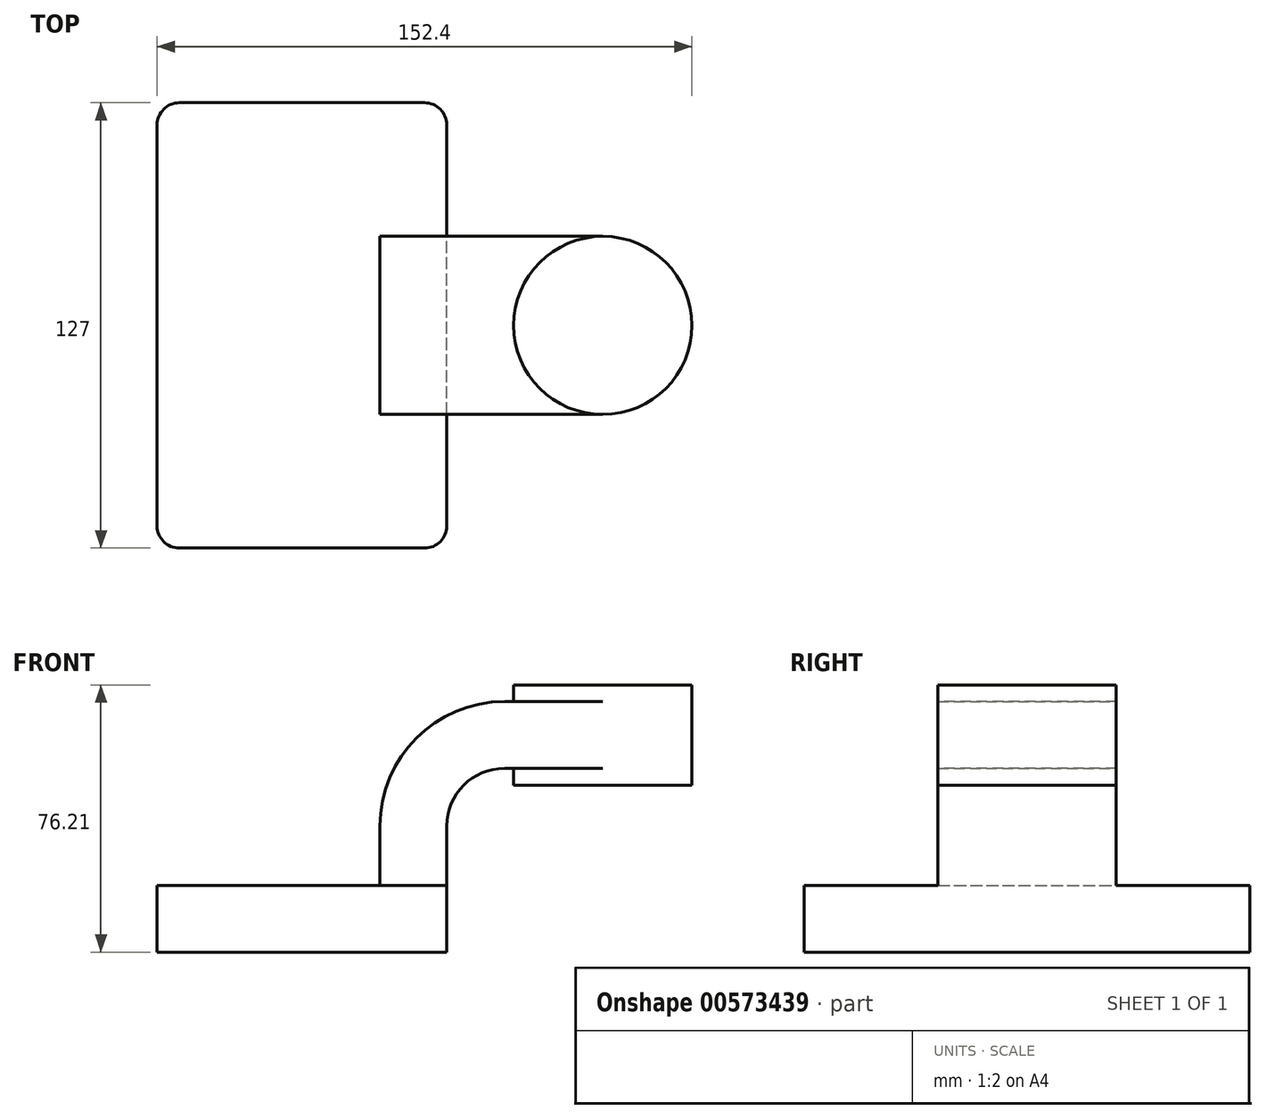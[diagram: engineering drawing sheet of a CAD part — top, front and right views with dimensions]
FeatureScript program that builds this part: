
annotation { "Feature Type Name" : "Feature", "Feature Type Description" : "" }
export const myFeature = defineFeature(function(context is Context, id is Id, definition is map)
    precondition{}
    {
        {
            var Q0;
            Q0=qCreatedBy(makeId("Front.planeOp"),FACE);
            var sketch = newSketch(context, id + "F0", { "sketchPlane" : qUnion([Q0])});
            skLineSegment(sketch, "E0.bottom", {"start": v(41.28, -9.52) * mm, "end": v(-41.28, -9.53) * mm});
            skLineSegment(sketch, "E0.top", {"start": v(41.28, 9.53) * mm, "end": v(-41.28, 9.53) * mm});
            skLineSegment(sketch, "E0.left", {"start": v(41.28, -9.52) * mm, "end": v(41.28, 9.53) * mm});
            skLineSegment(sketch, "E0.right", {"start": v(-41.28, -9.53) * mm, "end": v(-41.28, 9.53) * mm});
            skPoint(sketch, "E0.middle", {"position": v(0, 0) * mm});
            skLineSegment(sketch, "E1", {"start": v(41.28, 9.53) * mm, "end": v(41.28, 26.44) * mm});
            skLineSegment(sketch, "E2.bottom", {"start": v(111.12, 38.1) * mm, "end": v(60.32, 38.1) * mm});
            skLineSegment(sketch, "E2.top", {"start": v(111.12, 66.68) * mm, "end": v(60.32, 66.68) * mm});
            skLineSegment(sketch, "E2.left", {"start": v(111.12, 38.1) * mm, "end": v(111.12, 66.68) * mm});
            skLineSegment(sketch, "E2.right", {"start": v(60.32, 38.1) * mm, "end": v(60.32, 66.68) * mm});
            skPoint(sketch, "E2.middle", {"position": v(85.72, 52.39) * mm});
            skPoint(sketch, "E3.middle", {"position": v(111.12, 38.1) * mm});
            skLineSegment(sketch, "E4", {"start": v(15916.27, 15898.5) * mm, "end": v(15943.47, 15898.5) * mm});
            skArc(sketch, "E5", {"start": v(41.27, 26.44) * mm, "mid": v(46.09, 38.06) * mm, "end": v(57.7, 42.88) * mm});
            skLineSegment(sketch, "E6", {"start": v(57.7, 42.88) * mm, "end": v(85.72, 42.88) * mm});
            skPoint(sketch, "E6.endSnap0", {"position": v(85.72, 66.68) * mm});
            skLineSegment(sketch, "E7.0", {"start": v(57.7, 61.93) * mm, "end": v(85.72, 61.93) * mm});
            skArc(sketch, "E7.1", {"start": v(22.23, 26.44) * mm, "mid": v(32.62, 51.53) * mm, "end": v(57.7, 61.93) * mm});
            skLineSegment(sketch, "E7.2", {"start": v(22.22, 9.53) * mm, "end": v(22.22, 26.44) * mm});
            skFitSpline(sketch, "E8", {"points": [v(-41.28, 9.53) * mm, v(57.7, 61.93) * mm], "startDerivative": vector(-3.58, 69.63) * mm, "endDerivative": vector(173.12, -0.17) * mm});
            skLineSegment(sketch, "E9", {"start": v(85.72, 66.68) * mm, "end": v(85.72, 38.1) * mm});
            skSolve(sketch);
        }
        {
            var Q0;
            Q0=makeQuery(id+"F0.imprint","IMPRINT",FACE,{"disambiguationData":[TD([[makeQuery(id+"F0.imprint","IMPRINT",EDGE,{"derivedFrom":sQuery(id+"F0.wireOp",EDGE,"E0.bottom")}),-1.0]])]});
            extrude(context, id + "F1", {"entities" : qUnion([Q0]), "endBound" : BoundingType.SYMMETRIC, "depth" : 127 * mm, "offsetDistance" : 25.4 * mm});
        }
        {
            var Q0;
            {var subQ1=sQuery(id+"F0.wireOp",EDGE,"E1");Q0=makeQuery(id+"F0.imprint","IMPRINT",FACE,{"disambiguationData":[TD([[makeQuery(id+"F0.imprint","IMPRINT",EDGE,{"derivedFrom":subQ1}),1.0]])]});}
            var Q1;
            {var subQ0=sQuery(id+"F0.wireOp",EDGE,"E6");var subQ1=sQuery(id+"F0.wireOp",EDGE,"E2.right");var subQ2=makeQuery(id+"F0.imprint","INTERSECT",VERTEX,{"derivedFrom":[subQ1,subQ0]});Q1=makeQuery(id+"F0.imprint","IMPRINT",FACE,{"disambiguationData":[TD([[makeQuery(id+"F0.imprint","IMPRINT",EDGE,{"disambiguationData":[TD([[subQ2,-1.0]])],"derivedFrom":subQ1}),-1.0]])]});}
            extrude(context, id + "F2", {"entities" : qUnion([Q0, Q1]), "operationType" : NewBodyOperationType.ADD, "endBound" : BoundingType.SYMMETRIC, "depth" : 50.8 * mm, "offsetDistance" : 25.4 * mm});
        }
        {
            var Q0;
            Q0=makeQuery(id+"F0.imprint","IMPRINT",FACE,{"disambiguationData":[TD([[makeQuery(id+"F0.imprint","IMPRINT",EDGE,{"derivedFrom":sQuery(id+"F0.wireOp",EDGE,"E7.1")}),1.0]])]});
            extrude(context, id + "F3", {"entities" : qUnion([Q0]), "operationType" : NewBodyOperationType.ADD, "endBound" : BoundingType.SYMMETRIC, "depth" : 15.88 * mm, "offsetDistance" : 25.4 * mm});
        }
        {
            var Q0;
            {var subQ4=sQuery(id+"F0.wireOp",EDGE,"E2.left");Q0=makeQuery(id+"F0.imprint","IMPRINT",FACE,{"disambiguationData":[TD([[makeQuery(id+"F0.imprint","IMPRINT",EDGE,{"derivedFrom":subQ4}),1.0]])]});}
            var Q1;
            Q1=sQuery(id+"F0.wireOp",EDGE,"E9");
            revolve(context, id + "F4", {"operationType" : NewBodyOperationType.ADD, "entities" : qUnion([Q0]), "axis" : qUnion([Q1]), "revolveType" : RevolveType.FULL});
        }
        {
            var Q0;
            Q0=makeQuery(id+"F1.opExtrude","CAP_EDGE",EDGE,{"disambiguationData":[OSD([sQuery(id+"F0.wireOp",EDGE,"E0.right")])],"isStart":false});
            var Q1;
            Q1=makeQuery(id+"F1.opExtrude","CAP_EDGE",EDGE,{"disambiguationData":[OSD([sQuery(id+"F0.wireOp",EDGE,"E0.left")])],"isStart":false});
            var Q2;
            Q2=makeQuery(id+"F1.opExtrude","CAP_EDGE",EDGE,{"disambiguationData":[OSD([sQuery(id+"F0.wireOp",EDGE,"E0.left")])],"isStart":true});
            var Q3;
            Q3=makeQuery(id+"F1.opExtrude","CAP_EDGE",EDGE,{"disambiguationData":[OSD([sQuery(id+"F0.wireOp",EDGE,"E0.right")])],"isStart":true});
            fillet(context, id + "F5", {"entities" : qUnion([Q0, Q1, Q2, Q3]), "radius" : 6.35 * mm, "tangentPropagation" : true, "allowEdgeOverflow" : false});
        }
    });
